# Revit family: HydroTap_Assembled_Zip_Commercial_TouchFreeWave_CubeMixer_BCHA
name_source: partatom
category: Plumbing Fixtures
units: mm (PartAtom-declared; Revit-internal decimal feet)

## family parameters
Always vertical = Yes
Cut with Voids When Loaded = Yes
OmniClass Number = 23.21.21.25
OmniClass Title = Commercial Food and Beverage Dispensing Equipment
Part Type = Normal
Room Calculation Point = No
Round Connector Dimension = Use Diameter
Shared = No
Work Plane-Based = No

## types (4) — shared parameters
CW Connection = Yes
Electrical Connection = Yes
FixtureMaterial = Metal_Chrome_Zip
HW Connection = Yes
IfcExportAs = IfcElectricAppliance
IfcExportType = NOTDEFINED
Manufacturer = Zip Australia
ManufacturerOverallHeight = 333 mm  [stored 1.09252 ft]
ManufacturerURLProductSpecific = https://www.zipwater.com
ModifiedIssue = 20230123 $
URL = https://www.zipwater.com
Uniclass2015Code = Pr_40_70_23_42
Uniclass2015Title = Instant boiling and cold water taps
Uniclass2015Version = Products v1.17
Vent Connection = Yes

## per-type parameters (varying)
| type | Booster | ColdWaterOffset | CommandCentre | Description | ElectricalOffset | ManufacturerOverallDepth | ManufacturerOverallWidth | ManufacturerSpecCode | Model | Type Comments |
| 20 People - Chrome (H5W921Z00AU) | No | 15 mm  [stored 0.0492126 ft] | HydroTap_CommandCentre_Zip : 280w x 455d x 333h (BCHA) | Zip HydroTap Touch-Free Wave Boiling, Chilled, Filtered water uses smart infrared 100% touch-free operation that is activated with the Wave of a hand. The water system features a single under bench command centre including full colour interactive touch screen display with pin code protection and customisable settings including boiling water safety mode, 2 energy saving modes including ON/OFF timers and 2 hour sleep mode, 'Quiet' mode with automated intelligent fan speed adjustment, SteriTouch® antimicrobial protection impregnated into key water paths for enhanced hygiene, 100% water efficient air cooled technology, 0.2 micron water filtration, and a refillable CO2 cylinder. | 53 mm  [stored 0.173885 ft] | 455 mm | 280 mm  [stored 0.918635 ft] | H5W921Z00AU | 20 People - Chrome | HydroTap Wave & Cube Mixer BCHA - Chrome - 20 People |
| 60 People - Chrome (H5W923Z00AU) | No | 192 mm | HydroTap_CommandCentre_Zip : 394w x 464d x 333h (BCHA) | Zip HydroTap Touch-Free Wave Boiling, Chilled Filtered water uses smart infrared 100% touch-free operation that is activated with the Wave of a hand. The water system features a single under bench command centre including full colour interactive touch screen display with pin code protection and customisable settings including boiling water safety mode, 2 energy saving modes including ON/OFF timers and 2 hour sleep mode, 'Quiet' mode with automated intelligent fan speed adjustment, SteriTouch® antimicrobial protection impregnated into key water paths for enhanced hygiene, 100% water efficient air cooled technology, 0.2 micron water filtration, and a refillable CO2 cylinder. Easy to install integrated ventilation tray included. | 347 mm | 464 mm  [stored 1.52231 ft] | 394 mm  [stored 1.29265 ft] | H5W923Z00AU | 60 People - Chrome | HydroTap Wave & Cube Mixer BCHA - Chrome - 60 People |
| 40 People - Chrome (H5W922Z00AU) | No | 192 mm | HydroTap_CommandCentre_Zip : 394w x 464d x 333h (BCHA) | Zip HydroTap Touch-Free Wave Boiling, Chilled, Filtered water uses smart infrared 100% touch-free operation that is activated with the Wave of a hand. The water system features a single under bench command centre including full colour interactive touch screen display with pin code protection and customisable settings including boiling water safety mode, 2 energy saving modes including ON/OFF timers and 2 hour sleep mode, 'Quiet' mode with automated intelligent fan speed adjustment, SteriTouch® antimicrobial protection impregnated into key water paths for enhanced hygiene, 100% water efficient air cooled technology, 0.2 micron water filtration, and a refillable CO2 cylinder. Easy to install integrated ventilation tray included. | 347 mm | 464 mm  [stored 1.52231 ft] | 394 mm  [stored 1.29265 ft] | H5W922Z00AU | 40 People - Chrome | HydroTap Wave & Cube Mixer BCHA - Chrome - 40 People |
| 100 People - Chrome (H5W924Z00AU) | Yes | 192 mm | HydroTap_CommandCentre_Zip : 394w x 464d x 333h (BCHA) | Zip HydroTap Touch-Free Wave Boiling, Chilled, Filtered water uses smart infrared 100% touch-free operation that is activated with the Wave of a hand. The water system features a single under bench command centre including full colour interactive touch screen display with pin code protection and customisable settings including boiling water safety mode, 2 energy saving modes including ON/OFF timers and 2 hour sleep mode, 'Quiet' mode with automated intelligent fan speed adjustment, SteriTouch® antimicrobial protection impregnated into key water paths for enhanced hygiene, 100% water efficient air cooled technology, 0.2 micron water filtration, and a refillable CO2 cylinder. Easy to install integrated ventilation tray included. | 347 mm | 464 mm  [stored 1.52231 ft] | 394 mm  [stored 1.29265 ft] | H5W924Z00AU | 100 People - Chrome | HydroTap Wave & Cube Mixer BCHA - Chrome - 100 People |

note: [stored X ft] marks values corroborated as IEEE doubles in the binary element streams (Revit-internal decimal feet)

## geometry (parser evidence)
native form markers: Sweep x16
no freeform markers — native parametric forms only
